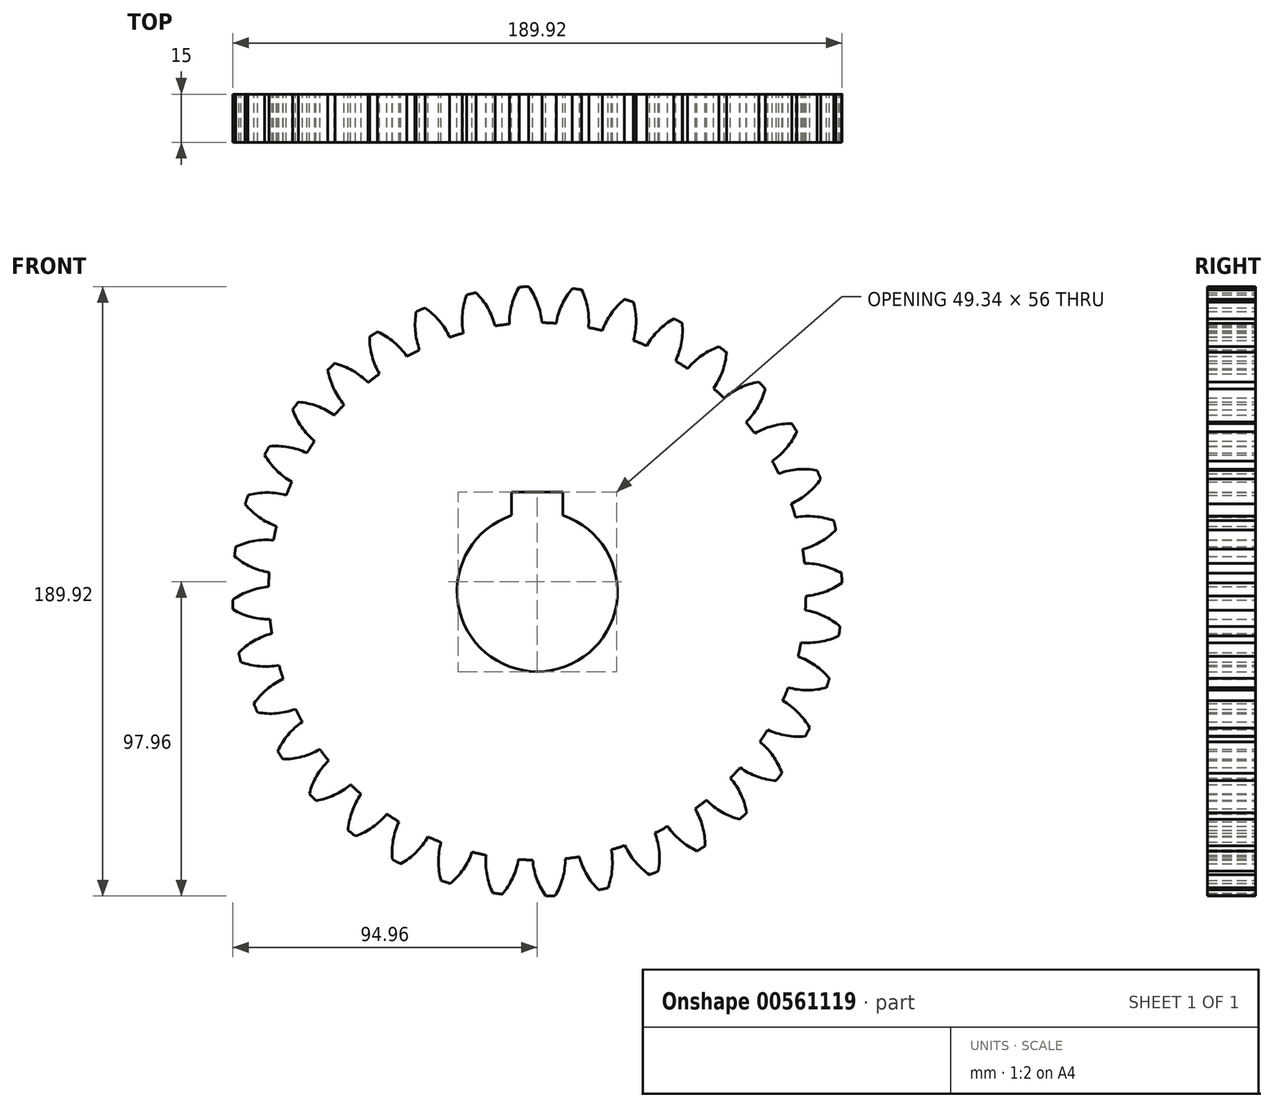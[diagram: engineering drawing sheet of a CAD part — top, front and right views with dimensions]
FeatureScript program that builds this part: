
annotation { "Feature Type Name" : "Feature", "Feature Type Description" : "" }
export const myFeature = defineFeature(function(context is Context, id is Id, definition is map)
    precondition{}
    {
        {
            var Q0;
            Q0=qCreatedBy(makeId("Front.planeOp"),FACE);
            var sketch = newSketch(context, id + "F0", { "sketchPlane" : qUnion([Q0])});
            skCircle(sketch, "E0", {"center": v(0, 0) * mm, "radius": 83.75 * mm});
            skCircle(sketch, "E1", {"center": v(0, 0) * mm, "radius": 90 * mm, "construction": true});
            skCircle(sketch, "E2", {"center": v(0, 0) * mm, "radius": 95 * mm, "construction": true});
            skLineSegment(sketch, "E3", {"start": v(0, 0) * mm, "end": v(0, 97.65) * mm, "construction": true});
            skLineSegment(sketch, "E4", {"start": v(0, 0) * mm, "end": v(-7.83, 179.33) * mm, "construction": true});
            skLineSegment(sketch, "E5", {"start": v(0, 90) * mm, "end": v(-217.65, 90) * mm, "construction": true});
            skLineSegment(sketch, "E6", {"start": v(0, 90) * mm, "end": v(-200.71, 16.95) * mm, "construction": true});
            skCircle(sketch, "E7", {"center": v(0, 0) * mm, "radius": 84.57 * mm, "construction": true});
            skCircle(sketch, "E8", {"center": v(0, 90) * mm, "radius": 22.5 * mm, "construction": true});
            skArc(sketch, "E9", {"start": v(0, 90) * mm, "mid": v(-1.18, 92.57) * mm, "end": v(-2.66, 94.96) * mm});
            skArc(sketch, "E10", {"start": v(1.43, 83.74) * mm, "mid": v(0.94, 86.92) * mm, "end": v(0, 90) * mm});
            skArc(sketch, "E11.MirrorCS", {"start": v(-8.72, 83.3) * mm, "mid": v(-8.5, 86.5) * mm, "end": v(-7.84, 89.66) * mm});
            skArc(sketch, "E12.MirrorCS", {"start": v(-7.84, 89.66) * mm, "mid": v(-6.9, 92.32) * mm, "end": v(-5.62, 94.83) * mm});
            skArc(sketch, "E13", {"start": v(-5.62, 94.83) * mm, "mid": v(-4.14, 94.9) * mm, "end": v(-2.66, 94.96) * mm});
            skSolve(sketch);
        }
        {
            var Q0;
            Q0 = qSketchRegion(id + "F0", true);
            extrude(context, id + "F1", {"entities" : qUnion([Q0]), "depth" : 15 * mm, "offsetDistance" : 25.4 * mm});
        }
        {
            var Q0;
            Q0=makeQuery(id+"F1.opExtrude","SWEPT_BODY",BODY,{"disambiguationData":[OSD([sQuery(id+"F0.wireOp",EDGE,"E0"),sQuery(id+"F0.wireOp",EDGE,"E9"),sQuery(id+"F0.wireOp",EDGE,"E10"),sQuery(id+"F0.wireOp",EDGE,"E11.MirrorCS"),sQuery(id+"F0.wireOp",EDGE,"E12.MirrorCS"),sQuery(id+"F0.wireOp",EDGE,"E13")])]});
            var Q1;
            Q1=makeQuery(id+"F1.opExtrude","SWEPT_FACE",FACE,{"disambiguationData":[OSD([sQuery(id+"F0.wireOp",EDGE,"E0")])]});
            circularPattern(context, id + "F2", {"entities" : qUnion([Q0]), "axis" : qUnion([Q1]), "angle" : 360 * degree, "instanceCount" : 36, "equalSpace" : true});
        }
        {
            var Q0;
            Q0=makeQuery(id+"F2.opPattern","COPY",BODY,{"derivedFrom":makeQuery(id+"F1.opExtrude","SWEPT_BODY",BODY,{"disambiguationData":[OSD([sQuery(id+"F0.wireOp",EDGE,"E0"),sQuery(id+"F0.wireOp",EDGE,"E9"),sQuery(id+"F0.wireOp",EDGE,"E10"),sQuery(id+"F0.wireOp",EDGE,"E11.MirrorCS"),sQuery(id+"F0.wireOp",EDGE,"E12.MirrorCS"),sQuery(id+"F0.wireOp",EDGE,"E13")])]}),"instanceName":"17"});
            var Q1;
            Q1=makeQuery(id+"F2.opPattern","COPY",BODY,{"derivedFrom":makeQuery(id+"F1.opExtrude","SWEPT_BODY",BODY,{"disambiguationData":[OSD([sQuery(id+"F0.wireOp",EDGE,"E0"),sQuery(id+"F0.wireOp",EDGE,"E9"),sQuery(id+"F0.wireOp",EDGE,"E10"),sQuery(id+"F0.wireOp",EDGE,"E11.MirrorCS"),sQuery(id+"F0.wireOp",EDGE,"E12.MirrorCS"),sQuery(id+"F0.wireOp",EDGE,"E13")])]}),"instanceName":"13"});
            var Q2;
            Q2=makeQuery(id+"F1.opExtrude","SWEPT_BODY",BODY,{"disambiguationData":[OSD([sQuery(id+"F0.wireOp",EDGE,"E0"),sQuery(id+"F0.wireOp",EDGE,"E9"),sQuery(id+"F0.wireOp",EDGE,"E10"),sQuery(id+"F0.wireOp",EDGE,"E11.MirrorCS"),sQuery(id+"F0.wireOp",EDGE,"E12.MirrorCS"),sQuery(id+"F0.wireOp",EDGE,"E13")])]});
            var Q3;
            Q3=makeQuery(id+"F2.opPattern","COPY",BODY,{"derivedFrom":makeQuery(id+"F1.opExtrude","SWEPT_BODY",BODY,{"disambiguationData":[OSD([sQuery(id+"F0.wireOp",EDGE,"E0"),sQuery(id+"F0.wireOp",EDGE,"E9"),sQuery(id+"F0.wireOp",EDGE,"E10"),sQuery(id+"F0.wireOp",EDGE,"E11.MirrorCS"),sQuery(id+"F0.wireOp",EDGE,"E12.MirrorCS"),sQuery(id+"F0.wireOp",EDGE,"E13")])]}),"instanceName":"7"});
            var Q4;
            Q4=makeQuery(id+"F2.opPattern","COPY",BODY,{"derivedFrom":makeQuery(id+"F1.opExtrude","SWEPT_BODY",BODY,{"disambiguationData":[OSD([sQuery(id+"F0.wireOp",EDGE,"E0"),sQuery(id+"F0.wireOp",EDGE,"E9"),sQuery(id+"F0.wireOp",EDGE,"E10"),sQuery(id+"F0.wireOp",EDGE,"E11.MirrorCS"),sQuery(id+"F0.wireOp",EDGE,"E12.MirrorCS"),sQuery(id+"F0.wireOp",EDGE,"E13")])]}),"instanceName":"18"});
            var Q5;
            Q5=makeQuery(id+"F2.opPattern","COPY",BODY,{"derivedFrom":makeQuery(id+"F1.opExtrude","SWEPT_BODY",BODY,{"disambiguationData":[OSD([sQuery(id+"F0.wireOp",EDGE,"E0"),sQuery(id+"F0.wireOp",EDGE,"E9"),sQuery(id+"F0.wireOp",EDGE,"E10"),sQuery(id+"F0.wireOp",EDGE,"E11.MirrorCS"),sQuery(id+"F0.wireOp",EDGE,"E12.MirrorCS"),sQuery(id+"F0.wireOp",EDGE,"E13")])]}),"instanceName":"3"});
            var Q6;
            Q6=makeQuery(id+"F2.opPattern","COPY",BODY,{"derivedFrom":makeQuery(id+"F1.opExtrude","SWEPT_BODY",BODY,{"disambiguationData":[OSD([sQuery(id+"F0.wireOp",EDGE,"E0"),sQuery(id+"F0.wireOp",EDGE,"E9"),sQuery(id+"F0.wireOp",EDGE,"E10"),sQuery(id+"F0.wireOp",EDGE,"E11.MirrorCS"),sQuery(id+"F0.wireOp",EDGE,"E12.MirrorCS"),sQuery(id+"F0.wireOp",EDGE,"E13")])]}),"instanceName":"16"});
            var Q7;
            Q7=makeQuery(id+"F2.opPattern","COPY",BODY,{"derivedFrom":makeQuery(id+"F1.opExtrude","SWEPT_BODY",BODY,{"disambiguationData":[OSD([sQuery(id+"F0.wireOp",EDGE,"E0"),sQuery(id+"F0.wireOp",EDGE,"E9"),sQuery(id+"F0.wireOp",EDGE,"E10"),sQuery(id+"F0.wireOp",EDGE,"E11.MirrorCS"),sQuery(id+"F0.wireOp",EDGE,"E12.MirrorCS"),sQuery(id+"F0.wireOp",EDGE,"E13")])]}),"instanceName":"8"});
            var Q8;
            Q8=makeQuery(id+"F2.opPattern","COPY",BODY,{"derivedFrom":makeQuery(id+"F1.opExtrude","SWEPT_BODY",BODY,{"disambiguationData":[OSD([sQuery(id+"F0.wireOp",EDGE,"E0"),sQuery(id+"F0.wireOp",EDGE,"E9"),sQuery(id+"F0.wireOp",EDGE,"E10"),sQuery(id+"F0.wireOp",EDGE,"E11.MirrorCS"),sQuery(id+"F0.wireOp",EDGE,"E12.MirrorCS"),sQuery(id+"F0.wireOp",EDGE,"E13")])]}),"instanceName":"19"});
            var Q9;
            Q9=makeQuery(id+"F2.opPattern","COPY",BODY,{"derivedFrom":makeQuery(id+"F1.opExtrude","SWEPT_BODY",BODY,{"disambiguationData":[OSD([sQuery(id+"F0.wireOp",EDGE,"E0"),sQuery(id+"F0.wireOp",EDGE,"E9"),sQuery(id+"F0.wireOp",EDGE,"E10"),sQuery(id+"F0.wireOp",EDGE,"E11.MirrorCS"),sQuery(id+"F0.wireOp",EDGE,"E12.MirrorCS"),sQuery(id+"F0.wireOp",EDGE,"E13")])]}),"instanceName":"1"});
            var Q10;
            Q10=makeQuery(id+"F2.opPattern","COPY",BODY,{"derivedFrom":makeQuery(id+"F1.opExtrude","SWEPT_BODY",BODY,{"disambiguationData":[OSD([sQuery(id+"F0.wireOp",EDGE,"E0"),sQuery(id+"F0.wireOp",EDGE,"E9"),sQuery(id+"F0.wireOp",EDGE,"E10"),sQuery(id+"F0.wireOp",EDGE,"E11.MirrorCS"),sQuery(id+"F0.wireOp",EDGE,"E12.MirrorCS"),sQuery(id+"F0.wireOp",EDGE,"E13")])]}),"instanceName":"34"});
            var Q11;
            Q11=makeQuery(id+"F2.opPattern","COPY",BODY,{"derivedFrom":makeQuery(id+"F1.opExtrude","SWEPT_BODY",BODY,{"disambiguationData":[OSD([sQuery(id+"F0.wireOp",EDGE,"E0"),sQuery(id+"F0.wireOp",EDGE,"E9"),sQuery(id+"F0.wireOp",EDGE,"E10"),sQuery(id+"F0.wireOp",EDGE,"E11.MirrorCS"),sQuery(id+"F0.wireOp",EDGE,"E12.MirrorCS"),sQuery(id+"F0.wireOp",EDGE,"E13")])]}),"instanceName":"33"});
            var Q12;
            Q12=makeQuery(id+"F2.opPattern","COPY",BODY,{"derivedFrom":makeQuery(id+"F1.opExtrude","SWEPT_BODY",BODY,{"disambiguationData":[OSD([sQuery(id+"F0.wireOp",EDGE,"E0"),sQuery(id+"F0.wireOp",EDGE,"E9"),sQuery(id+"F0.wireOp",EDGE,"E10"),sQuery(id+"F0.wireOp",EDGE,"E11.MirrorCS"),sQuery(id+"F0.wireOp",EDGE,"E12.MirrorCS"),sQuery(id+"F0.wireOp",EDGE,"E13")])]}),"instanceName":"32"});
            var Q13;
            Q13=makeQuery(id+"F2.opPattern","COPY",BODY,{"derivedFrom":makeQuery(id+"F1.opExtrude","SWEPT_BODY",BODY,{"disambiguationData":[OSD([sQuery(id+"F0.wireOp",EDGE,"E0"),sQuery(id+"F0.wireOp",EDGE,"E9"),sQuery(id+"F0.wireOp",EDGE,"E10"),sQuery(id+"F0.wireOp",EDGE,"E11.MirrorCS"),sQuery(id+"F0.wireOp",EDGE,"E12.MirrorCS"),sQuery(id+"F0.wireOp",EDGE,"E13")])]}),"instanceName":"31"});
            var Q14;
            Q14=makeQuery(id+"F2.opPattern","COPY",BODY,{"derivedFrom":makeQuery(id+"F1.opExtrude","SWEPT_BODY",BODY,{"disambiguationData":[OSD([sQuery(id+"F0.wireOp",EDGE,"E0"),sQuery(id+"F0.wireOp",EDGE,"E9"),sQuery(id+"F0.wireOp",EDGE,"E10"),sQuery(id+"F0.wireOp",EDGE,"E11.MirrorCS"),sQuery(id+"F0.wireOp",EDGE,"E12.MirrorCS"),sQuery(id+"F0.wireOp",EDGE,"E13")])]}),"instanceName":"30"});
            var Q15;
            Q15=makeQuery(id+"F2.opPattern","COPY",BODY,{"derivedFrom":makeQuery(id+"F1.opExtrude","SWEPT_BODY",BODY,{"disambiguationData":[OSD([sQuery(id+"F0.wireOp",EDGE,"E0"),sQuery(id+"F0.wireOp",EDGE,"E9"),sQuery(id+"F0.wireOp",EDGE,"E10"),sQuery(id+"F0.wireOp",EDGE,"E11.MirrorCS"),sQuery(id+"F0.wireOp",EDGE,"E12.MirrorCS"),sQuery(id+"F0.wireOp",EDGE,"E13")])]}),"instanceName":"29"});
            var Q16;
            Q16=makeQuery(id+"F2.opPattern","COPY",BODY,{"derivedFrom":makeQuery(id+"F1.opExtrude","SWEPT_BODY",BODY,{"disambiguationData":[OSD([sQuery(id+"F0.wireOp",EDGE,"E0"),sQuery(id+"F0.wireOp",EDGE,"E9"),sQuery(id+"F0.wireOp",EDGE,"E10"),sQuery(id+"F0.wireOp",EDGE,"E11.MirrorCS"),sQuery(id+"F0.wireOp",EDGE,"E12.MirrorCS"),sQuery(id+"F0.wireOp",EDGE,"E13")])]}),"instanceName":"28"});
            var Q17;
            Q17=makeQuery(id+"F2.opPattern","COPY",BODY,{"derivedFrom":makeQuery(id+"F1.opExtrude","SWEPT_BODY",BODY,{"disambiguationData":[OSD([sQuery(id+"F0.wireOp",EDGE,"E0"),sQuery(id+"F0.wireOp",EDGE,"E9"),sQuery(id+"F0.wireOp",EDGE,"E10"),sQuery(id+"F0.wireOp",EDGE,"E11.MirrorCS"),sQuery(id+"F0.wireOp",EDGE,"E12.MirrorCS"),sQuery(id+"F0.wireOp",EDGE,"E13")])]}),"instanceName":"27"});
            var Q18;
            Q18=makeQuery(id+"F2.opPattern","COPY",BODY,{"derivedFrom":makeQuery(id+"F1.opExtrude","SWEPT_BODY",BODY,{"disambiguationData":[OSD([sQuery(id+"F0.wireOp",EDGE,"E0"),sQuery(id+"F0.wireOp",EDGE,"E9"),sQuery(id+"F0.wireOp",EDGE,"E10"),sQuery(id+"F0.wireOp",EDGE,"E11.MirrorCS"),sQuery(id+"F0.wireOp",EDGE,"E12.MirrorCS"),sQuery(id+"F0.wireOp",EDGE,"E13")])]}),"instanceName":"26"});
            var Q19;
            Q19=makeQuery(id+"F2.opPattern","COPY",BODY,{"derivedFrom":makeQuery(id+"F1.opExtrude","SWEPT_BODY",BODY,{"disambiguationData":[OSD([sQuery(id+"F0.wireOp",EDGE,"E0"),sQuery(id+"F0.wireOp",EDGE,"E9"),sQuery(id+"F0.wireOp",EDGE,"E10"),sQuery(id+"F0.wireOp",EDGE,"E11.MirrorCS"),sQuery(id+"F0.wireOp",EDGE,"E12.MirrorCS"),sQuery(id+"F0.wireOp",EDGE,"E13")])]}),"instanceName":"25"});
            var Q20;
            Q20=makeQuery(id+"F2.opPattern","COPY",BODY,{"derivedFrom":makeQuery(id+"F1.opExtrude","SWEPT_BODY",BODY,{"disambiguationData":[OSD([sQuery(id+"F0.wireOp",EDGE,"E0"),sQuery(id+"F0.wireOp",EDGE,"E9"),sQuery(id+"F0.wireOp",EDGE,"E10"),sQuery(id+"F0.wireOp",EDGE,"E11.MirrorCS"),sQuery(id+"F0.wireOp",EDGE,"E12.MirrorCS"),sQuery(id+"F0.wireOp",EDGE,"E13")])]}),"instanceName":"23"});
            var Q21;
            Q21=makeQuery(id+"F2.opPattern","COPY",BODY,{"derivedFrom":makeQuery(id+"F1.opExtrude","SWEPT_BODY",BODY,{"disambiguationData":[OSD([sQuery(id+"F0.wireOp",EDGE,"E0"),sQuery(id+"F0.wireOp",EDGE,"E9"),sQuery(id+"F0.wireOp",EDGE,"E10"),sQuery(id+"F0.wireOp",EDGE,"E11.MirrorCS"),sQuery(id+"F0.wireOp",EDGE,"E12.MirrorCS"),sQuery(id+"F0.wireOp",EDGE,"E13")])]}),"instanceName":"5"});
            var Q22;
            Q22=makeQuery(id+"F2.opPattern","COPY",BODY,{"derivedFrom":makeQuery(id+"F1.opExtrude","SWEPT_BODY",BODY,{"disambiguationData":[OSD([sQuery(id+"F0.wireOp",EDGE,"E0"),sQuery(id+"F0.wireOp",EDGE,"E9"),sQuery(id+"F0.wireOp",EDGE,"E10"),sQuery(id+"F0.wireOp",EDGE,"E11.MirrorCS"),sQuery(id+"F0.wireOp",EDGE,"E12.MirrorCS"),sQuery(id+"F0.wireOp",EDGE,"E13")])]}),"instanceName":"2"});
            var Q23;
            Q23=makeQuery(id+"F2.opPattern","COPY",BODY,{"derivedFrom":makeQuery(id+"F1.opExtrude","SWEPT_BODY",BODY,{"disambiguationData":[OSD([sQuery(id+"F0.wireOp",EDGE,"E0"),sQuery(id+"F0.wireOp",EDGE,"E9"),sQuery(id+"F0.wireOp",EDGE,"E10"),sQuery(id+"F0.wireOp",EDGE,"E11.MirrorCS"),sQuery(id+"F0.wireOp",EDGE,"E12.MirrorCS"),sQuery(id+"F0.wireOp",EDGE,"E13")])]}),"instanceName":"9"});
            var Q24;
            Q24=makeQuery(id+"F2.opPattern","COPY",BODY,{"derivedFrom":makeQuery(id+"F1.opExtrude","SWEPT_BODY",BODY,{"disambiguationData":[OSD([sQuery(id+"F0.wireOp",EDGE,"E0"),sQuery(id+"F0.wireOp",EDGE,"E9"),sQuery(id+"F0.wireOp",EDGE,"E10"),sQuery(id+"F0.wireOp",EDGE,"E11.MirrorCS"),sQuery(id+"F0.wireOp",EDGE,"E12.MirrorCS"),sQuery(id+"F0.wireOp",EDGE,"E13")])]}),"instanceName":"22"});
            var Q25;
            Q25=makeQuery(id+"F2.opPattern","COPY",BODY,{"derivedFrom":makeQuery(id+"F1.opExtrude","SWEPT_BODY",BODY,{"disambiguationData":[OSD([sQuery(id+"F0.wireOp",EDGE,"E0"),sQuery(id+"F0.wireOp",EDGE,"E9"),sQuery(id+"F0.wireOp",EDGE,"E10"),sQuery(id+"F0.wireOp",EDGE,"E11.MirrorCS"),sQuery(id+"F0.wireOp",EDGE,"E12.MirrorCS"),sQuery(id+"F0.wireOp",EDGE,"E13")])]}),"instanceName":"24"});
            var Q26;
            Q26=makeQuery(id+"F2.opPattern","COPY",BODY,{"derivedFrom":makeQuery(id+"F1.opExtrude","SWEPT_BODY",BODY,{"disambiguationData":[OSD([sQuery(id+"F0.wireOp",EDGE,"E0"),sQuery(id+"F0.wireOp",EDGE,"E9"),sQuery(id+"F0.wireOp",EDGE,"E10"),sQuery(id+"F0.wireOp",EDGE,"E11.MirrorCS"),sQuery(id+"F0.wireOp",EDGE,"E12.MirrorCS"),sQuery(id+"F0.wireOp",EDGE,"E13")])]}),"instanceName":"35"});
            var Q27;
            Q27=makeQuery(id+"F2.opPattern","COPY",BODY,{"derivedFrom":makeQuery(id+"F1.opExtrude","SWEPT_BODY",BODY,{"disambiguationData":[OSD([sQuery(id+"F0.wireOp",EDGE,"E0"),sQuery(id+"F0.wireOp",EDGE,"E9"),sQuery(id+"F0.wireOp",EDGE,"E10"),sQuery(id+"F0.wireOp",EDGE,"E11.MirrorCS"),sQuery(id+"F0.wireOp",EDGE,"E12.MirrorCS"),sQuery(id+"F0.wireOp",EDGE,"E13")])]}),"instanceName":"12"});
            var Q28;
            Q28=makeQuery(id+"F2.opPattern","COPY",BODY,{"derivedFrom":makeQuery(id+"F1.opExtrude","SWEPT_BODY",BODY,{"disambiguationData":[OSD([sQuery(id+"F0.wireOp",EDGE,"E0"),sQuery(id+"F0.wireOp",EDGE,"E9"),sQuery(id+"F0.wireOp",EDGE,"E10"),sQuery(id+"F0.wireOp",EDGE,"E11.MirrorCS"),sQuery(id+"F0.wireOp",EDGE,"E12.MirrorCS"),sQuery(id+"F0.wireOp",EDGE,"E13")])]}),"instanceName":"10"});
            var Q29;
            Q29=makeQuery(id+"F2.opPattern","COPY",BODY,{"derivedFrom":makeQuery(id+"F1.opExtrude","SWEPT_BODY",BODY,{"disambiguationData":[OSD([sQuery(id+"F0.wireOp",EDGE,"E0"),sQuery(id+"F0.wireOp",EDGE,"E9"),sQuery(id+"F0.wireOp",EDGE,"E10"),sQuery(id+"F0.wireOp",EDGE,"E11.MirrorCS"),sQuery(id+"F0.wireOp",EDGE,"E12.MirrorCS"),sQuery(id+"F0.wireOp",EDGE,"E13")])]}),"instanceName":"6"});
            var Q30;
            Q30=makeQuery(id+"F2.opPattern","COPY",BODY,{"derivedFrom":makeQuery(id+"F1.opExtrude","SWEPT_BODY",BODY,{"disambiguationData":[OSD([sQuery(id+"F0.wireOp",EDGE,"E0"),sQuery(id+"F0.wireOp",EDGE,"E9"),sQuery(id+"F0.wireOp",EDGE,"E10"),sQuery(id+"F0.wireOp",EDGE,"E11.MirrorCS"),sQuery(id+"F0.wireOp",EDGE,"E12.MirrorCS"),sQuery(id+"F0.wireOp",EDGE,"E13")])]}),"instanceName":"11"});
            var Q31;
            Q31=makeQuery(id+"F2.opPattern","COPY",BODY,{"derivedFrom":makeQuery(id+"F1.opExtrude","SWEPT_BODY",BODY,{"disambiguationData":[OSD([sQuery(id+"F0.wireOp",EDGE,"E0"),sQuery(id+"F0.wireOp",EDGE,"E9"),sQuery(id+"F0.wireOp",EDGE,"E10"),sQuery(id+"F0.wireOp",EDGE,"E11.MirrorCS"),sQuery(id+"F0.wireOp",EDGE,"E12.MirrorCS"),sQuery(id+"F0.wireOp",EDGE,"E13")])]}),"instanceName":"14"});
            var Q32;
            Q32=makeQuery(id+"F2.opPattern","COPY",BODY,{"derivedFrom":makeQuery(id+"F1.opExtrude","SWEPT_BODY",BODY,{"disambiguationData":[OSD([sQuery(id+"F0.wireOp",EDGE,"E0"),sQuery(id+"F0.wireOp",EDGE,"E9"),sQuery(id+"F0.wireOp",EDGE,"E10"),sQuery(id+"F0.wireOp",EDGE,"E11.MirrorCS"),sQuery(id+"F0.wireOp",EDGE,"E12.MirrorCS"),sQuery(id+"F0.wireOp",EDGE,"E13")])]}),"instanceName":"4"});
            var Q33;
            Q33=makeQuery(id+"F2.opPattern","COPY",BODY,{"derivedFrom":makeQuery(id+"F1.opExtrude","SWEPT_BODY",BODY,{"disambiguationData":[OSD([sQuery(id+"F0.wireOp",EDGE,"E0"),sQuery(id+"F0.wireOp",EDGE,"E9"),sQuery(id+"F0.wireOp",EDGE,"E10"),sQuery(id+"F0.wireOp",EDGE,"E11.MirrorCS"),sQuery(id+"F0.wireOp",EDGE,"E12.MirrorCS"),sQuery(id+"F0.wireOp",EDGE,"E13")])]}),"instanceName":"21"});
            var Q34;
            Q34=makeQuery(id+"F2.opPattern","COPY",BODY,{"derivedFrom":makeQuery(id+"F1.opExtrude","SWEPT_BODY",BODY,{"disambiguationData":[OSD([sQuery(id+"F0.wireOp",EDGE,"E0"),sQuery(id+"F0.wireOp",EDGE,"E9"),sQuery(id+"F0.wireOp",EDGE,"E10"),sQuery(id+"F0.wireOp",EDGE,"E11.MirrorCS"),sQuery(id+"F0.wireOp",EDGE,"E12.MirrorCS"),sQuery(id+"F0.wireOp",EDGE,"E13")])]}),"instanceName":"20"});
            var Q35;
            Q35=makeQuery(id+"F2.opPattern","COPY",BODY,{"derivedFrom":makeQuery(id+"F1.opExtrude","SWEPT_BODY",BODY,{"disambiguationData":[OSD([sQuery(id+"F0.wireOp",EDGE,"E0"),sQuery(id+"F0.wireOp",EDGE,"E9"),sQuery(id+"F0.wireOp",EDGE,"E10"),sQuery(id+"F0.wireOp",EDGE,"E11.MirrorCS"),sQuery(id+"F0.wireOp",EDGE,"E12.MirrorCS"),sQuery(id+"F0.wireOp",EDGE,"E13")])]}),"instanceName":"15"});
            booleanBodies(context, id + "F3", {"operationType" : BooleanOperationType.UNION, "tools" : qUnion([Q0, Q1, Q2, Q3, Q4, Q5, Q6, Q7, Q8, Q9, Q10, Q11, Q12, Q13, Q14, Q15, Q16, Q17, Q18, Q19, Q20, Q21, Q22, Q23, Q24, Q25, Q26, Q27, Q28, Q29, Q30, Q31, Q32, Q33, Q34, Q35])});
        }
        {
            var Q0;
            {var subQ0=makeQuery(id+"F1.opExtrude","CAP_FACE",FACE,{"disambiguationData":[OSD([sQuery(id+"F0.wireOp",EDGE,"E0"),sQuery(id+"F0.wireOp",EDGE,"E9"),sQuery(id+"F0.wireOp",EDGE,"E10"),sQuery(id+"F0.wireOp",EDGE,"E11.MirrorCS"),sQuery(id+"F0.wireOp",EDGE,"E12.MirrorCS"),sQuery(id+"F0.wireOp",EDGE,"E13")])],"isStart":true});Q0=makeQuery(id+"F3.opBoolean","MERGE",FACE,{"derivedFrom":[subQ0,makeQuery(id+"F2.opPattern","COPY",FACE,{"derivedFrom":subQ0,"instanceName":"1"}),makeQuery(id+"F2.opPattern","COPY",FACE,{"derivedFrom":subQ0,"instanceName":"2"}),makeQuery(id+"F2.opPattern","COPY",FACE,{"derivedFrom":subQ0,"instanceName":"3"}),makeQuery(id+"F2.opPattern","COPY",FACE,{"derivedFrom":subQ0,"instanceName":"4"}),makeQuery(id+"F2.opPattern","COPY",FACE,{"derivedFrom":subQ0,"instanceName":"5"}),makeQuery(id+"F2.opPattern","COPY",FACE,{"derivedFrom":subQ0,"instanceName":"6"}),makeQuery(id+"F2.opPattern","COPY",FACE,{"derivedFrom":subQ0,"instanceName":"7"}),makeQuery(id+"F2.opPattern","COPY",FACE,{"derivedFrom":subQ0,"instanceName":"8"}),makeQuery(id+"F2.opPattern","COPY",FACE,{"derivedFrom":subQ0,"instanceName":"9"}),makeQuery(id+"F2.opPattern","COPY",FACE,{"derivedFrom":subQ0,"instanceName":"10"}),makeQuery(id+"F2.opPattern","COPY",FACE,{"derivedFrom":subQ0,"instanceName":"11"}),makeQuery(id+"F2.opPattern","COPY",FACE,{"derivedFrom":subQ0,"instanceName":"12"}),makeQuery(id+"F2.opPattern","COPY",FACE,{"derivedFrom":subQ0,"instanceName":"13"}),makeQuery(id+"F2.opPattern","COPY",FACE,{"derivedFrom":subQ0,"instanceName":"14"}),makeQuery(id+"F2.opPattern","COPY",FACE,{"derivedFrom":subQ0,"instanceName":"15"}),makeQuery(id+"F2.opPattern","COPY",FACE,{"derivedFrom":subQ0,"instanceName":"16"}),makeQuery(id+"F2.opPattern","COPY",FACE,{"derivedFrom":subQ0,"instanceName":"17"}),makeQuery(id+"F2.opPattern","COPY",FACE,{"derivedFrom":subQ0,"instanceName":"18"}),makeQuery(id+"F2.opPattern","COPY",FACE,{"derivedFrom":subQ0,"instanceName":"19"}),makeQuery(id+"F2.opPattern","COPY",FACE,{"derivedFrom":subQ0,"instanceName":"20"}),makeQuery(id+"F2.opPattern","COPY",FACE,{"derivedFrom":subQ0,"instanceName":"21"}),makeQuery(id+"F2.opPattern","COPY",FACE,{"derivedFrom":subQ0,"instanceName":"22"}),makeQuery(id+"F2.opPattern","COPY",FACE,{"derivedFrom":subQ0,"instanceName":"23"}),makeQuery(id+"F2.opPattern","COPY",FACE,{"derivedFrom":subQ0,"instanceName":"24"}),makeQuery(id+"F2.opPattern","COPY",FACE,{"derivedFrom":subQ0,"instanceName":"25"}),makeQuery(id+"F2.opPattern","COPY",FACE,{"derivedFrom":subQ0,"instanceName":"26"}),makeQuery(id+"F2.opPattern","COPY",FACE,{"derivedFrom":subQ0,"instanceName":"27"}),makeQuery(id+"F2.opPattern","COPY",FACE,{"derivedFrom":subQ0,"instanceName":"28"}),makeQuery(id+"F2.opPattern","COPY",FACE,{"derivedFrom":subQ0,"instanceName":"29"}),makeQuery(id+"F2.opPattern","COPY",FACE,{"derivedFrom":subQ0,"instanceName":"30"}),makeQuery(id+"F2.opPattern","COPY",FACE,{"derivedFrom":subQ0,"instanceName":"31"}),makeQuery(id+"F2.opPattern","COPY",FACE,{"derivedFrom":subQ0,"instanceName":"32"}),makeQuery(id+"F2.opPattern","COPY",FACE,{"derivedFrom":subQ0,"instanceName":"33"}),makeQuery(id+"F2.opPattern","COPY",FACE,{"derivedFrom":subQ0,"instanceName":"34"}),makeQuery(id+"F2.opPattern","COPY",FACE,{"derivedFrom":subQ0,"instanceName":"35"})]});}
            var sketch = newSketch(context, id + "F4", { "sketchPlane" : qUnion([Q0])});
            skCircle(sketch, "E14", {"center": v(0, 0) * mm, "radius": 25 * mm});
            skLineSegment(sketch, "E15.bottom", {"start": v(-8, 31) * mm, "end": v(8, 31) * mm});
            skLineSegment(sketch, "E15.top", {"start": v(-8, 19) * mm, "end": v(8, 19) * mm});
            skLineSegment(sketch, "E15.left", {"start": v(-8, 31) * mm, "end": v(-8, 19) * mm});
            skLineSegment(sketch, "E15.right", {"start": v(8, 31) * mm, "end": v(8, 19) * mm});
            skSolve(sketch);
        }
        {
            var Q0;
            Q0 = qSketchRegion(id + "F4", true);
            extrude(context, id + "F5", {"entities" : qUnion([Q0]), "operationType" : NewBodyOperationType.REMOVE, "oppositeDirection" : true, "depth" : 25.4 * mm, "offsetDistance" : 25.4 * mm});
        }
    });
